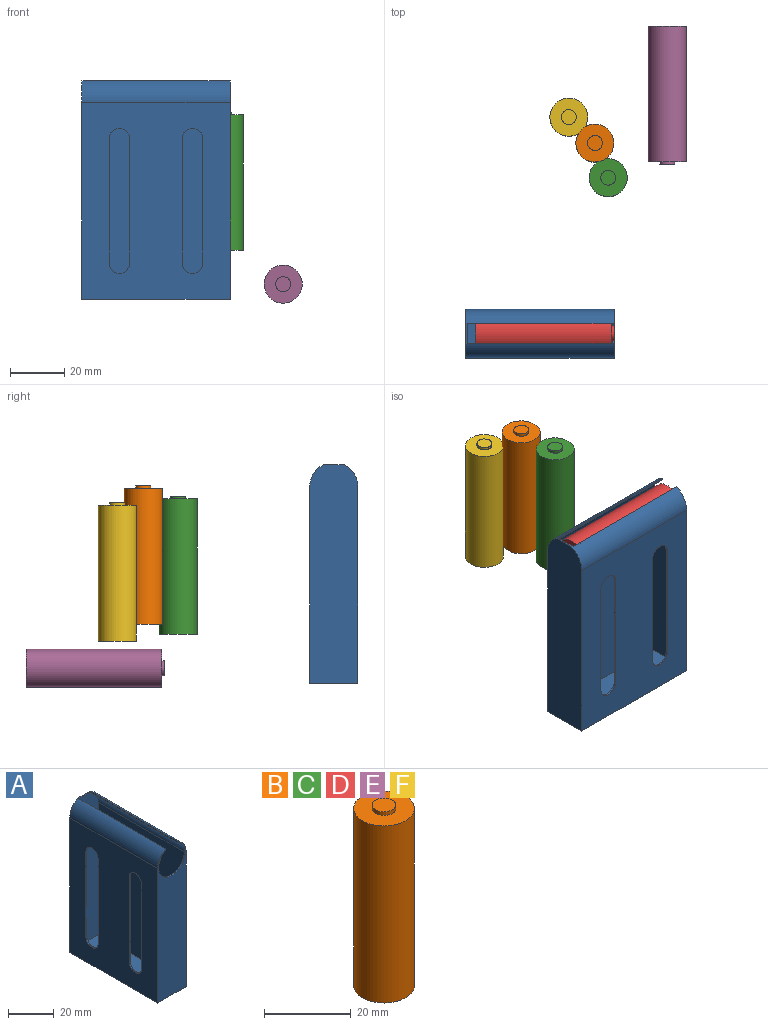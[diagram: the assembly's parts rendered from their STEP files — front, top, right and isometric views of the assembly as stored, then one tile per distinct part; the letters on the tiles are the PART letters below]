
ASSEMBLY  parts=6 mates=1
PART A: 24 faces, bbox 17.8x54.6x80.4 mm
  f0: plane 53.98x0.71mm, normal (-1,0,0), area 38.3mm2, adj f1,f3,f9,f13
  f1: cylinder r=8.26mm len=53.98mm, axis (0,-1,0), area 988.7mm2, adj f0,f2,f3,f4,f5,f9,f10
  f2: plane 53.98x0.71mm, normal (1,0,0), area 38.3mm2, adj f1,f3,f9,f14
  f3: plane 79.15x16.51mm, normal (0,-1,0), area 1281.8mm2, adj f0,f1,f2,f4,f10,f12,f15
  f4: plane 71.12x53.34mm, normal (-1,0,0), area 3793.5mm2, adj f1,f3,f5,f12
  f5: plane 71.12x16.51mm, normal (0,1,0), area 1067.1mm2, adj f1,f4,f10,f12
  f6: plane 72.39x54.61mm, normal (1,0,0), area 3953.2mm2, adj f7,f9,f11,f13
  f7: plane 80.42x17.78mm, normal (0,1,0), area 1406.8mm2, adj f6,f8,f11,f13,f14,f15
  f8: plane 72.39x54.61mm, normal (-1,0,0), area 3165.2mm2, adj f7,f9,f11,f14,f16,f17,f18,f19
  f9: plane 80.42x17.78mm, normal (0,-1,0), area 1192.1mm2, adj f0,f1,f2,f6,f8,f11,f13,f14
  f10: plane 71.12x53.34mm, normal (1,0,0), area 3005.6mm2, adj f1,f3,f5,f12,f16,f17,f18,f19
  f11: plane 54.61x17.78mm, normal (0,0,-1), area 971mm2, adj f6,f7,f8,f9
  f12: plane 53.34x16.51mm, normal (0,0,1), area 880.6mm2, adj f3,f4,f5,f10
  f13: cylinder r=8.89mm len=54.61mm, axis (0,-1,0), area 547.6mm2, adj f0,f6,f7,f9,f15
  f14: cylinder r=8.89mm len=54.61mm, axis (0,-1,0), area 547.6mm2, adj f2,f7,f8,f9,f15
  f15: plane 7.62x0.64mm, normal (0,0,1), area 4.8mm2, adj f3,f7,f13,f14
  f16: cylinder r=3.81mm len=7.62mm, axis (-1,0,0), area 7.6mm2, adj f8,f10,f17,f19
  f17: plane 45.72x0.64mm, normal (0,1,0), area 29mm2, adj f8,f10,f16,f18
  f18: cylinder r=3.81mm len=7.62mm, axis (-1,0,0), area 7.6mm2, adj f8,f10,f17,f19
  f19: plane 45.72x0.64mm, normal (0,-1,0), area 29mm2, adj f8,f10,f16,f18
  f20: cylinder r=3.81mm len=7.62mm, axis (-1,0,0), area 7.6mm2, adj f8,f10,f21,f23
  f21: plane 45.72x0.64mm, normal (0,1,0), area 29mm2, adj f8,f10,f20,f22
  f22: cylinder r=3.81mm len=7.62mm, axis (-1,0,0), area 7.6mm2, adj f8,f10,f21,f23
  f23: plane 45.72x0.64mm, normal (0,-1,0), area 29mm2, adj f8,f10,f20,f22
PART B: 5 faces, bbox 14x14x51 mm
  f0: cylinder r=7mm len=50mm, axis (0,0,-1), area 2199.1mm2, adj f1,f2
  f1: plane 14x14mm, normal (0,0,1), area 130.2mm2, adj f0,f3
  f2: plane 14x14mm, normal (0,0,-1), area 153.9mm2, adj f0
  f3: cylinder r=2.75mm len=5.5mm, axis (0,0,-1), area 17.3mm2, adj f1,f4
  f4: plane 5.5x5.5mm, normal (0,0,1), area 23.8mm2, adj f3
PART C: same geometry as B
PART D: same geometry as B
PART E: same geometry as B
PART F: same geometry as B
PLACE A rot(axis=(0,0,1),90deg) t=(-32.9,-3.06,-8.03)mm fixed
PLACE B t=(-12.66,67.1,13.63)mm
PLACE C t=(-7.76,54.34,9.92)mm
PLACE D rot(axis=(0.58,0.58,0.58),120deg) t=(-56.5,-3.06,64.36)mm
PLACE E rot(axis=(1,0,0),90deg) t=(13.96,110.31,-2.48)mm
PLACE F t=(-22.26,76.66,7.5)mm
MATE slider D.f0 <-> A.f13  axis (1,0,0) through (-6.5,-3.06,64.36)mm
